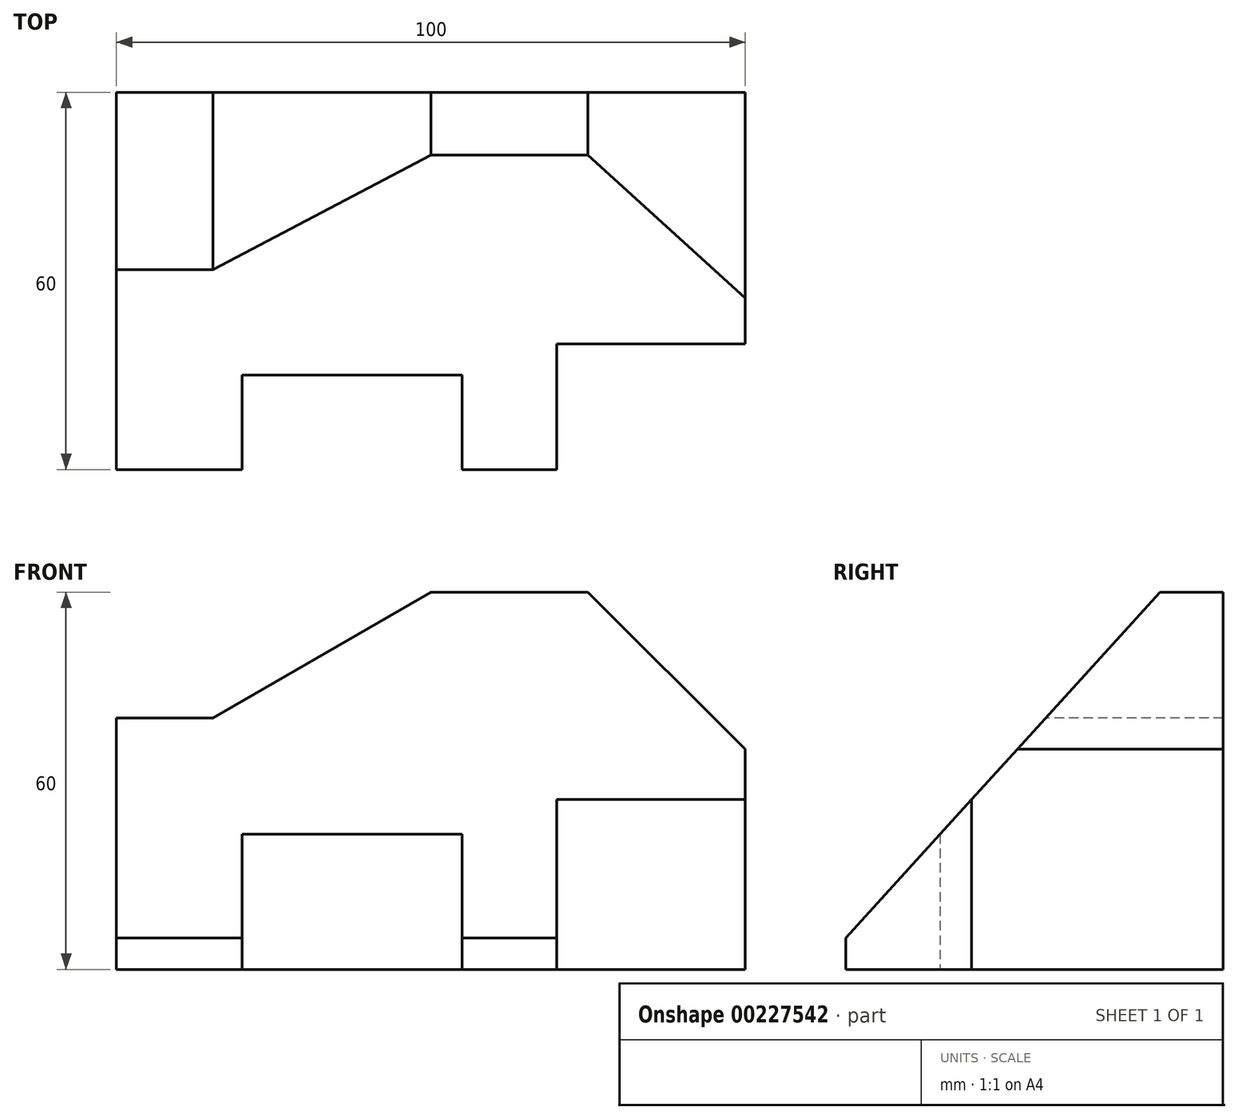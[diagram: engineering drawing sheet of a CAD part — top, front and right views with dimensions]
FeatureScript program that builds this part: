
annotation { "Feature Type Name" : "Feature", "Feature Type Description" : "" }
export const myFeature = defineFeature(function(context is Context, id is Id, definition is map)
    precondition{}
    {
        {
            var Q0;
            Q0=qCreatedBy(makeId("Top.planeOp"),FACE);
            var sketch = newSketch(context, id + "F0", { "sketchPlane" : qUnion([Q0])});
            skLineSegment(sketch, "E0", {"start": v(0, 0) * mm, "end": v(0, 60) * mm});
            skLineSegment(sketch, "E1", {"start": v(0, 60) * mm, "end": v(100, 60) * mm});
            skLineSegment(sketch, "E2", {"start": v(100, 60) * mm, "end": v(100, 20) * mm});
            skLineSegment(sketch, "E3", {"start": v(100, 20) * mm, "end": v(70, 20) * mm});
            skLineSegment(sketch, "E4", {"start": v(70, 20) * mm, "end": v(70, 0) * mm});
            skLineSegment(sketch, "E5", {"start": v(70, 0) * mm, "end": v(55, 0) * mm});
            skLineSegment(sketch, "E6", {"start": v(20, 15) * mm, "end": v(20, 0) * mm});
            skLineSegment(sketch, "E7", {"start": v(20, 0) * mm, "end": v(0, 0) * mm});
            skLineSegment(sketch, "E8", {"start": v(55, 0) * mm, "end": v(55, 15) * mm});
            skLineSegment(sketch, "E9", {"start": v(55, 15) * mm, "end": v(20, 15) * mm});
            skSolve(sketch);
        }
        {
            var Q0;
            Q0 = qSketchRegion(id + "F0", true);
            extrude(context, id + "F1", {"entities" : qUnion([Q0]), "depth" : 60 * mm});
        }
        {
            var Q0;
            Q0=makeQuery(id+"F1.opExtrude","SWEPT_FACE",FACE,{"disambiguationData":[OSD([sQuery(id+"F0.wireOp",EDGE,"E7")])]});
            var sketch = newSketch(context, id + "F2", { "sketchPlane" : qUnion([Q0])});
            skPoint(sketch, "E10.0", {"position": v(0, 60) * mm});
            skPoint(sketch, "E11.0", {"position": v(100, 60) * mm});
            skLineSegment(sketch, "E12.0", {"start": v(20, 60) * mm, "end": v(0, 60) * mm, "construction": true});
            skPoint(sketch, "E13.0", {"position": v(62.5, 60) * mm});
            skLineSegment(sketch, "E14.0", {"start": v(100, 60) * mm, "end": v(70, 60) * mm, "construction": true});
            skLineSegment(sketch, "E15.0", {"start": v(55, 60) * mm, "end": v(20, 60) * mm, "construction": true});
            skLineSegment(sketch, "E16.0", {"start": v(70, 60) * mm, "end": v(55, 60) * mm, "construction": true});
            skLineSegment(sketch, "E17.0", {"start": v(0, 60) * mm, "end": v(0, 0) * mm, "construction": true});
            skLineSegment(sketch, "E18", {"start": v(50, 60) * mm, "end": v(15.36, 40) * mm});
            skLineSegment(sketch, "E19", {"start": v(15.36, 40) * mm, "end": v(0, 40) * mm});
            skLineSegment(sketch, "E20", {"start": v(0, 40) * mm, "end": v(0, 60) * mm});
            skLineSegment(sketch, "E21", {"start": v(50, 60) * mm, "end": v(0, 60) * mm});
            skLineSegment(sketch, "E22.0", {"start": v(100, 60) * mm, "end": v(100, 0) * mm, "construction": true});
            skLineSegment(sketch, "E23", {"start": v(75, 60) * mm, "end": v(100, 35) * mm});
            skLineSegment(sketch, "E24", {"start": v(75, 60) * mm, "end": v(100, 60) * mm});
            skLineSegment(sketch, "E25", {"start": v(100, 35) * mm, "end": v(100, 60) * mm});
            skSolve(sketch);
        }
        {
            var Q0;
            Q0 = qSketchRegion(id + "F2", true);
            extrude(context, id + "F3", {"entities" : qUnion([Q0]), "operationType" : NewBodyOperationType.REMOVE, "endBound" : BoundingType.THROUGH_ALL, "oppositeDirection" : true, "depth" : 25 * mm});
        }
        {
            var Q0;
            Q0=qCreatedBy(makeId("Right.planeOp"),FACE);
            var sketch = newSketch(context, id + "F4", { "sketchPlane" : qUnion([Q0])});
            skLineSegment(sketch, "E26.0.0", {"start": v(0, 0) * mm, "end": v(20, 0) * mm, "construction": true});
            skLineSegment(sketch, "E26.0.1", {"start": v(20, 0) * mm, "end": v(20, 60) * mm, "construction": true});
            skLineSegment(sketch, "E26.0.2", {"start": v(20, 60) * mm, "end": v(0, 60) * mm, "construction": true});
            skLineSegment(sketch, "E27", {"start": v(50, 60) * mm, "end": v(0, 5) * mm});
            skLineSegment(sketch, "E28", {"start": v(0, 5) * mm, "end": v(0, 60) * mm});
            skLineSegment(sketch, "E29", {"start": v(0, 60) * mm, "end": v(0, 5) * mm});
            skLineSegment(sketch, "E30", {"start": v(0, 60) * mm, "end": v(50, 60) * mm});
            skLineSegment(sketch, "E31", {"start": v(50, 60) * mm, "end": v(0, 60) * mm});
            skLineSegment(sketch, "E32.0", {"start": v(60, 35) * mm, "end": v(60, 60) * mm, "construction": true});
            skLineSegment(sketch, "E33.0", {"start": v(60, 35) * mm, "end": v(60, 0) * mm, "construction": true});
            skLineSegment(sketch, "E34.0", {"start": v(60, 0) * mm, "end": v(20, 0) * mm, "construction": true});
            skLineSegment(sketch, "E35.0.3", {"start": v(0, 60) * mm, "end": v(0, 0) * mm, "construction": true});
            skLineSegment(sketch, "E36.0", {"start": v(60, 35) * mm, "end": v(20, 35) * mm, "construction": true});
            skLineSegment(sketch, "E37.0.0", {"start": v(60, 0) * mm, "end": v(60, 35) * mm, "construction": true});
            skLineSegment(sketch, "E37.0.2", {"start": v(20, 35) * mm, "end": v(20, 0) * mm, "construction": true});
            skLineSegment(sketch, "E37.0.3", {"start": v(20, 0) * mm, "end": v(60, 0) * mm, "construction": true});
            skLineSegment(sketch, "E38.0.0", {"start": v(20, 60) * mm, "end": v(20, 35) * mm, "construction": true});
            skLineSegment(sketch, "E38.0.1", {"start": v(20, 35) * mm, "end": v(60, 35) * mm, "construction": true});
            skLineSegment(sketch, "E38.0.3", {"start": v(60, 60) * mm, "end": v(20, 60) * mm, "construction": true});
            skSolve(sketch);
        }
        {
            var Q0;
            Q0=makeQuery(id+"F4.imprint","IMPRINT",FACE,{"disambiguationData":[TD([[makeQuery(id+"F4.imprint","IMPRINT",EDGE,{"derivedFrom":sQuery(id+"F4.wireOp",EDGE,"E27")}),-1.0]])]});
            extrude(context, id + "F5", {"entities" : qUnion([Q0]), "operationType" : NewBodyOperationType.REMOVE, "endBound" : BoundingType.THROUGH_ALL, "depth" : 25 * mm});
        }
    });
